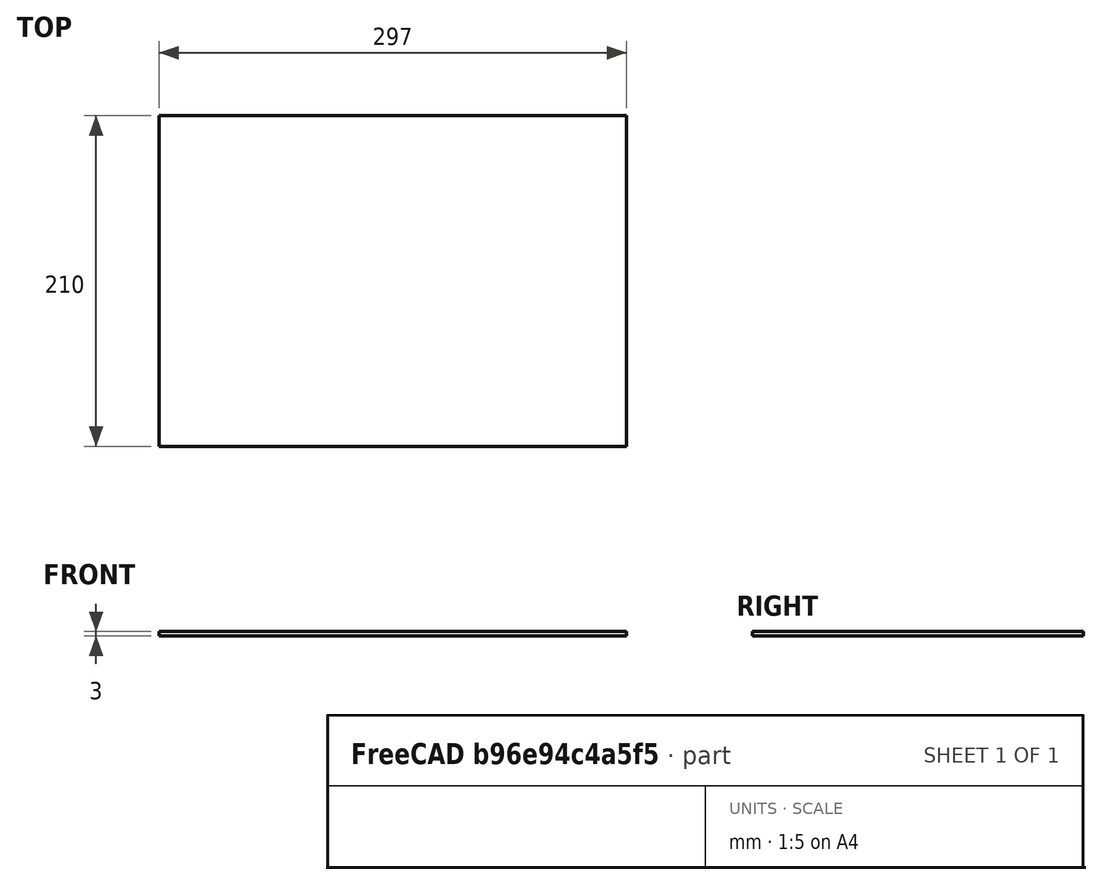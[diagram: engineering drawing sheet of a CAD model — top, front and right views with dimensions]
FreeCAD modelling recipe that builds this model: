
FCSTD DOCUMENT  (FreeCAD 0.20R29177 (Git))
Label: 1001_keyboard_PCB_Wood_stencil_A4
License: All rights reserved
LicenseURL: http://en.wikipedia.org/wiki/All_rights_reserved
objects: Sketcher::SketchObject×2, PartDesign::Pad×1, PartDesign::Body×1
note: 5 computed .brp shape members not serialized (recipe doc carries the construction recipe); baked Part::Feature solids carry a one-line shape summary decoded from their .brp

FEATURE [Sketcher::SketchObject] Sketch
  FullyConstrained = true
  MapMode = 5
  Support = -> [XY_Plane]
  sketch-geometry (5):
    g0: LineSegment StartX=0 StartY=210 StartZ=0 EndX=297 EndY=210 EndZ=0
    g1: LineSegment StartX=297 StartY=210 StartZ=0 EndX=297 EndY=0 EndZ=0
    g2: LineSegment StartX=297 StartY=0 StartZ=0 EndX=0 EndY=0 EndZ=0
    g3: LineSegment StartX=0 StartY=0 StartZ=0 EndX=0 EndY=105 EndZ=0
    g4: LineSegment StartX=0 StartY=105 StartZ=0 EndX=0 EndY=210 EndZ=0
  constraints (14):
    c: Coincident(g0,g1)
    c: Coincident(g1,g2)
    c: Horizontal(g0)
    c: Horizontal(g2)
    c: Vertical(g1)
    c: DistanceY(g1,g1) = 210
    c: DistanceX(g0,g0) = 297
    c: Coincident(g3,g2)
    c: Coincident(g4,g0)
    c: Equal(g3,g4)
    c: Vertical(g4)
    c: Vertical(g3)
    c: Coincident(g3,g4)
    c: Coincident(g2,g-1)
FEATURE [PartDesign::Pad] Pad  label="A4_Landscape"
  AllowMultiFace = false
  Direction = (0,0,1)
  Length = 3
  Length2 = 100
  Profile = -> Sketch
  ReferenceAxis = -> Sketch [N_Axis]
  Type = 0
FEATURE [PartDesign::Body] Body
  Group = -> [Sketch,Pad]
  Origin = -> Origin
  Tip = -> Pad
FEATURE [Sketcher::SketchObject] Sketch010  label="PCB002_Analog"
  FullyConstrained = false
  MapMode = 5
  Support = -> [XY_Plane]
  sketch-geometry (35):
    g0: LineSegment StartX=225.828 StartY=165.494 StartZ=0 EndX=185.828 EndY=165.494 EndZ=0
    g1: LineSegment StartX=225.828 StartY=165.494 StartZ=0 EndX=265.828 EndY=165.494 EndZ=0
    g2: LineSegment StartX=225.828 StartY=165.494 StartZ=0 EndX=225.828 EndY=182.994 EndZ=0
    g3: LineSegment StartX=225.828 StartY=165.494 StartZ=0 EndX=225.828 EndY=147.994 EndZ=0
    g4: LineSegment StartX=225.828 StartY=182.994 StartZ=0 EndX=185.828 EndY=182.994 EndZ=0
    g5: LineSegment StartX=185.828 StartY=182.994 StartZ=0 EndX=185.828 EndY=165.494 EndZ=0
    g6: LineSegment StartX=185.828 StartY=165.494 StartZ=0 EndX=185.828 EndY=147.994 EndZ=0
    g7: LineSegment StartX=185.828 StartY=147.994 StartZ=0 EndX=225.828 EndY=147.994 EndZ=0
    g8: LineSegment StartX=225.828 StartY=147.994 StartZ=0 EndX=265.828 EndY=147.994 EndZ=0
    g9: LineSegment StartX=265.828 StartY=147.994 StartZ=0 EndX=265.828 EndY=165.494 EndZ=0
    g10: LineSegment StartX=265.828 StartY=165.494 StartZ=0 EndX=265.828 EndY=182.994 EndZ=0
    g11: LineSegment StartX=265.828 StartY=182.994 StartZ=0 EndX=225.828 EndY=182.994 EndZ=0
    g12: Circle CenterX=265.828 CenterY=147.994 CenterZ=0 NormalX=0 NormalY=0 NormalZ=1 AngleXU=0 Radius=1
    g13: Circle CenterX=265.828 CenterY=182.994 CenterZ=0 NormalX=0 NormalY=0 NormalZ=1 AngleXU=0 Radius=1
    g14: Circle CenterX=185.828 CenterY=182.994 CenterZ=0 NormalX=0 NormalY=0 NormalZ=1 AngleXU=0 Radius=1
    g15: Circle CenterX=185.828 CenterY=147.994 CenterZ=0 NormalX=0 NormalY=0 NormalZ=1 AngleXU=0 Radius=1
    g16: LineSegment StartX=175.828 StartY=187.994 StartZ=0 EndX=175.828 EndY=160.494 EndZ=0
    g17: LineSegment StartX=175.828 StartY=160.494 StartZ=0 EndX=175.828 EndY=132.994 EndZ=0
    g18: LineSegment StartX=175.828 StartY=132.994 StartZ=0 EndX=225.828 EndY=132.994 EndZ=0
    g19: LineSegment StartX=225.828 StartY=132.994 StartZ=0 EndX=275.828 EndY=132.994 EndZ=0
    g20: LineSegment StartX=275.828 StartY=187.994 StartZ=0 EndX=225.828 EndY=187.994 EndZ=0
    g21: LineSegment StartX=225.828 StartY=187.994 StartZ=0 EndX=175.828 EndY=187.994 EndZ=0
    g22: Circle CenterX=180.828 CenterY=182.994 CenterZ=0 NormalX=0 NormalY=0 NormalZ=1 AngleXU=0 Radius=1.5
    g23: Circle CenterX=270.828 CenterY=182.994 CenterZ=0 NormalX=0 NormalY=0 NormalZ=1 AngleXU=0 Radius=1.5
    g24: Circle CenterX=270.828 CenterY=137.994 CenterZ=0 NormalX=0 NormalY=0 NormalZ=1 AngleXU=0 Radius=1.5
    g25: Circle CenterX=180.828 CenterY=137.994 CenterZ=0 NormalX=0 NormalY=0 NormalZ=1 AngleXU=0 Radius=1.5
    g26: LineSegment StartX=275.828 StartY=187.994 StartZ=0 EndX=275.828 EndY=174.085 EndZ=0
    g27: LineSegment StartX=275.828 StartY=174.085 StartZ=0 EndX=280.828 EndY=174.085 EndZ=0
    g28: LineSegment StartX=280.828 StartY=174.085 StartZ=0 EndX=280.828 EndY=165.494 EndZ=0
    g29: LineSegment StartX=280.828 StartY=165.494 StartZ=0 EndX=280.828 EndY=156.903 EndZ=0
    g30: LineSegment StartX=280.828 StartY=156.903 StartZ=0 EndX=275.828 EndY=156.903 EndZ=0
    g31: LineSegment StartX=225.828 StartY=132.994 StartZ=0 EndX=225.828 EndY=137.994 EndZ=0
    g32: LineSegment StartX=180.828 StartY=137.994 StartZ=0 EndX=225.828 EndY=137.994 EndZ=0
    g33: LineSegment StartX=225.828 StartY=137.994 StartZ=0 EndX=270.828 EndY=137.994 EndZ=0
    g34: LineSegment StartX=275.828 StartY=156.903 StartZ=0 EndX=275.828 EndY=132.994 EndZ=0
  constraints (89):
    c: Horizontal(g0)
    c: Coincident(g1,g0)
    c: Horizontal(g1)
    c: Coincident(g2,g0)
    c: Vertical(g2)
    c: Coincident(g3,g0)
    c: Vertical(g3)
    c: Equal(g1,g0)
    c: Equal(g3,g2)
    c: Coincident(g4,g2)
    c: Horizontal(g4)
    c: Coincident(g5,g4)
    c: Coincident(g5,g0)
    c: Vertical(g5)
    c: Coincident(g6,g5)
    c: Vertical(g6)
    c: Coincident(g7,g6)
    c: Coincident(g7,g3)
    c: Coincident(g8,g7)
    c: Coincident(g9,g8)
    c: Coincident(g9,g1)
    c: Vertical(g10)
    c: Coincident(g11,g10)
    c: Coincident(g11,g4)
    c: Horizontal(g11)
    c: Horizontal(g8)
    c: Horizontal(g7)
    c: Vertical(g9)
    c: DistanceX(g4,g10) = 80
    c: Coincident(g9,g10)
    c: DistanceY(g6,g4) = 35
    c: Coincident(g12,g8)
    c: Coincident(g13,g10)
    c: Coincident(g14,g4)
    c: Coincident(g15,g6)
    c: Equal(g12,g13)
    c: Equal(g13,g14)
    c: Equal(g14,g15)
    c: Vertical(g16)
    c: Coincident(g17,g16)
    c: Vertical(g17)
    c: Coincident(g18,g17)
    c: Horizontal(g18)
    c: Coincident(g19,g18)
    c: Horizontal(g20)
    c: Coincident(g21,g20)
    c: Coincident(g21,g16)
    c: Horizontal(g21)
    c: Vertical(g20,g2)
    c: Vertical(g3,g18)
    c: Horizontal(g19)
    c: Equal(g16,g17)
    c: Equal(g21,g20)
    c: Equal(g25,g24)
    c: Equal(g24,g23)
    c: Equal(g23,g22)
    c: Horizontal(g22,g23)
    c: Vertical(g23,g24)
    c: Horizontal(g24,g25)
    c: Vertical(g25,g22)
    c: DistanceX(g16,g20) = 100
    c: DistanceY(g17,g16) = 55
    c: Horizontal(g14,g22)
    c: DistanceY(g25,g22) = 45
    c: DistanceX(g25,g24) = 90
    c: Coincident(g27,g26)
    c: Horizontal(g27)
    c: Coincident(g28,g27)
    c: Vertical(g28)
    c: Coincident(g29,g28)
    c: Vertical(g29)
    c: Coincident(g30,g29)
    c: Horizontal(g30)
    c: Horizontal(g28,g1)
    c: Equal(g29,g28)
    c: Coincident(g31,g18)
    c: Horizontal(g31,g25)
    c: Vertical(g31)
    c: Coincident(g32,g25)
    c: Coincident(g32,g31)
    c: Coincident(g33,g31)
    c: Coincident(g33,g24)
    c: Equal(g33,g32)
    c: Coincident(g34,g30)
    c: Coincident(g34,g19)
    c: Vertical(g34)
    c: Coincident(g26,g20)
    c: Vertical(g26)
    c: Equal(g19,g20)
